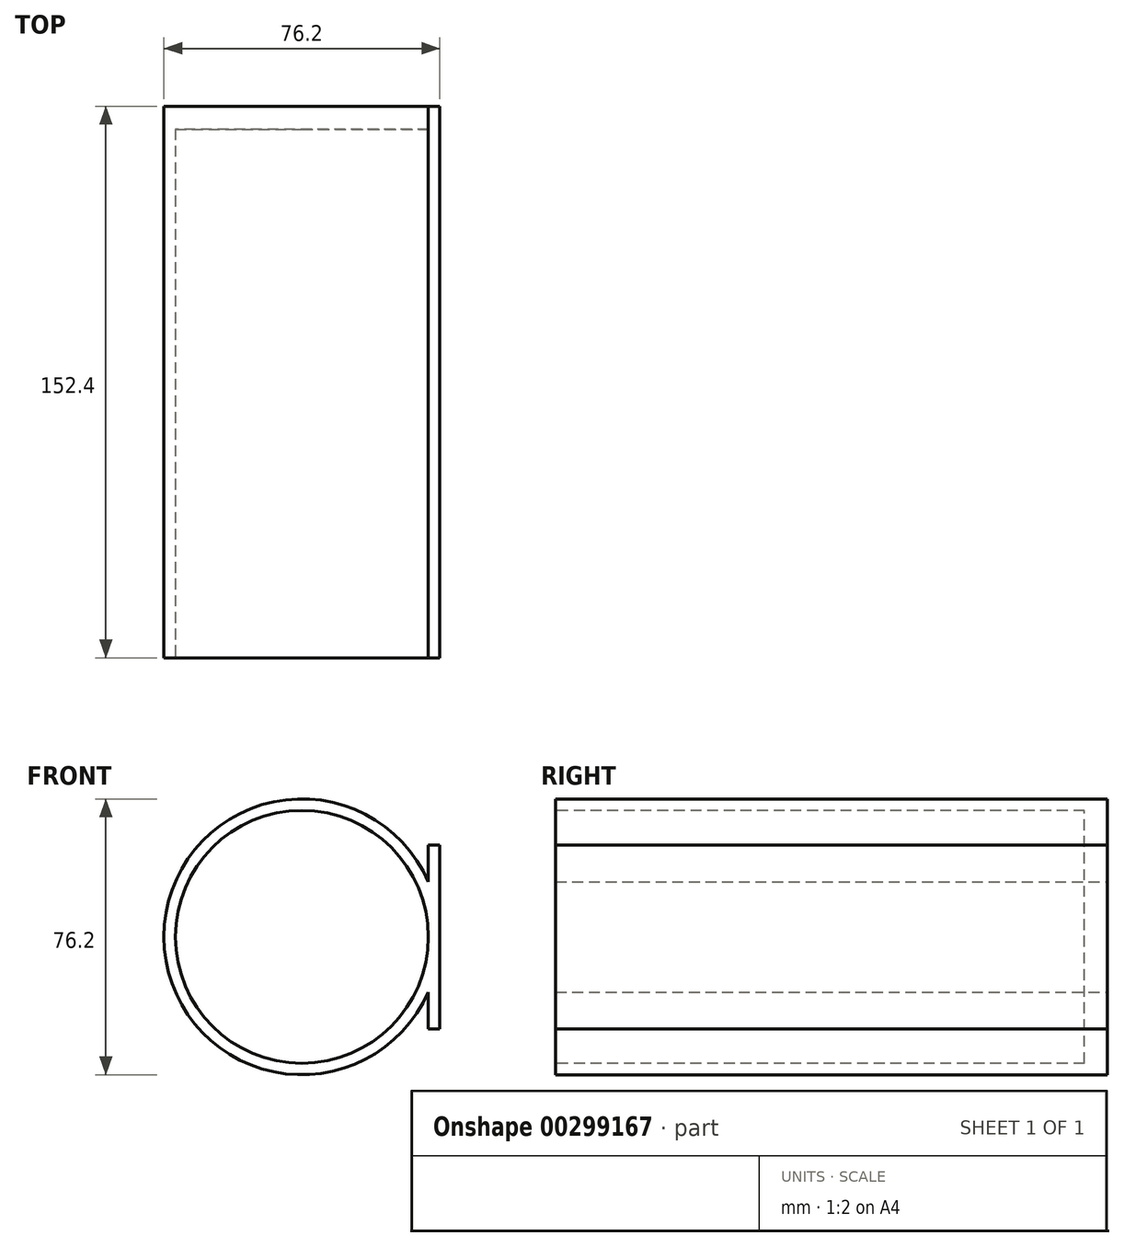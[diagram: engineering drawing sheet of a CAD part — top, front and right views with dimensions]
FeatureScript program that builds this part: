
annotation { "Feature Type Name" : "Feature", "Feature Type Description" : "" }
export const myFeature = defineFeature(function(context is Context, id is Id, definition is map)
    precondition{}
    {
        {
            var Q0;
            Q0=qCreatedBy(makeId("Front.planeOp"),FACE);
            var sketch = newSketch(context, id + "F0", { "sketchPlane" : qUnion([Q0])});
            skCircle(sketch, "E0", {"center": v(0, 0) * mm, "radius": 38.1 * mm});
            skSolve(sketch);
        }
        {
            var Q0;
            Q0 = qSketchRegion(id + "F0", true);
            extrude(context, id + "F1", {"entities" : qUnion([Q0]), "endBound" : BoundingType.SYMMETRIC, "depth" : 152.4 * mm});
        }
        {
            var Q0;
            Q0=makeQuery(id+"F1.opExtrude","CAP_FACE",FACE,{"disambiguationData":[OSD([sQuery(id+"F0.wireOp",EDGE,"E0")])],"isStart":false});
            var sketch = newSketch(context, id + "F2", { "sketchPlane" : qUnion([Q0])});
            skCircle(sketch, "E1", {"center": v(0, 0) * mm, "radius": 34.93 * mm});
            skSolve(sketch);
        }
        {
            var Q0;
            Q0 = qSketchRegion(id + "F2", true);
            extrude(context, id + "F3", {"entities" : qUnion([Q0]), "operationType" : NewBodyOperationType.REMOVE, "oppositeDirection" : true, "depth" : 146.05 * mm});
        }
        {
            var Q0;
            Q0=qCreatedBy(makeId("Top.planeOp"),FACE);
            var sketch = newSketch(context, id + "F4", { "sketchPlane" : qUnion([Q0])});
            skLineSegment(sketch, "E2", {"start": v(38.1, 76.2) * mm, "end": v(38.1, -76.2) * mm, "construction": true});
            skLineSegment(sketch, "E3", {"start": v(-38.1, -76.2) * mm, "end": v(-38.1, 76.2) * mm, "construction": true});
            skLineSegment(sketch, "E4", {"start": v(-34.93, -76.2) * mm, "end": v(-34.93, 69.85) * mm, "construction": true});
            skLineSegment(sketch, "E5", {"start": v(34.93, 69.85) * mm, "end": v(34.93, -76.2) * mm, "construction": true});
            skLineSegment(sketch, "E6.bottom", {"start": v(38.1, 76.2) * mm, "end": v(34.93, 76.2) * mm});
            skLineSegment(sketch, "E6.top", {"start": v(38.1, -76.2) * mm, "end": v(34.93, -76.2) * mm});
            skLineSegment(sketch, "E6.left", {"start": v(38.1, 76.2) * mm, "end": v(38.1, -76.2) * mm});
            skLineSegment(sketch, "E6.right", {"start": v(34.93, 76.2) * mm, "end": v(34.93, -76.2) * mm});
            skSolve(sketch);
        }
        {
            var Q0;
            Q0 = qSketchRegion(id + "F4", true);
            extrude(context, id + "F5", {"entities" : qUnion([Q0]), "operationType" : NewBodyOperationType.ADD, "endBound" : BoundingType.SYMMETRIC, "depth" : 50.8 * mm});
        }
    });
